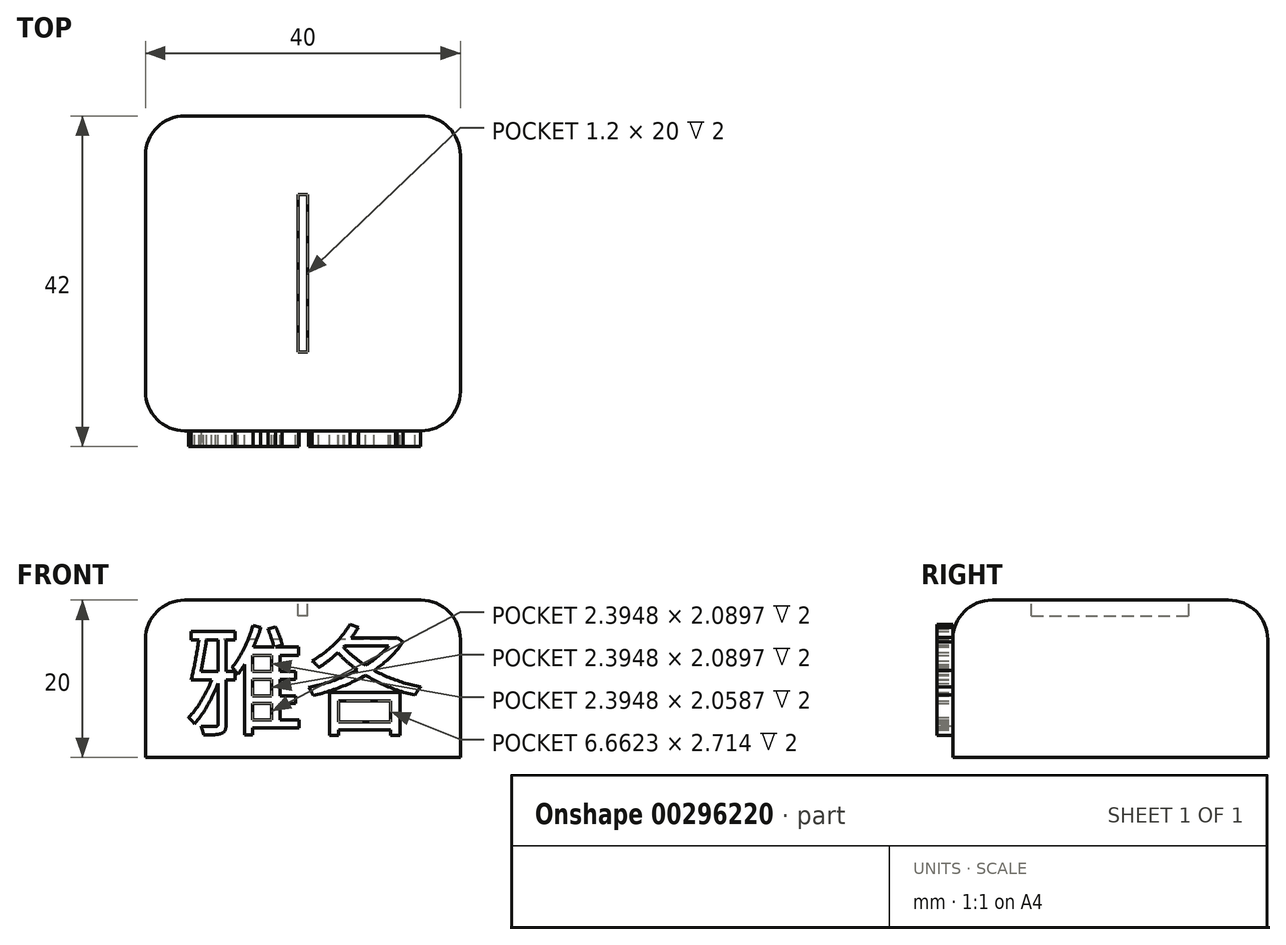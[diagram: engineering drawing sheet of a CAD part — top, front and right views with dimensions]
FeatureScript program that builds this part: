
annotation { "Feature Type Name" : "Feature", "Feature Type Description" : "" }
export const myFeature = defineFeature(function(context is Context, id is Id, definition is map)
    precondition{}
    {
        {
            var Q0;
            Q0=qCreatedBy(makeId("Top.planeOp"),FACE);
            var sketch = newSketch(context, id + "F0", { "sketchPlane" : qUnion([Q0])});
            skLineSegment(sketch, "E0.bottom", {"start": v(20, -20) * mm, "end": v(-20, -20) * mm});
            skLineSegment(sketch, "E0.top", {"start": v(20, 20) * mm, "end": v(-20, 20) * mm});
            skLineSegment(sketch, "E0.left", {"start": v(20, -20) * mm, "end": v(20, 20) * mm});
            skLineSegment(sketch, "E0.right", {"start": v(-20, -20) * mm, "end": v(-20, 20) * mm});
            skPoint(sketch, "E0.middle", {"position": v(0, 0) * mm});
            skLineSegment(sketch, "E1.bottom", {"start": v(0.6, -10) * mm, "end": v(-0.6, -10) * mm});
            skLineSegment(sketch, "E1.top", {"start": v(0.6, 10) * mm, "end": v(-0.6, 10) * mm});
            skLineSegment(sketch, "E1.left", {"start": v(0.6, -10) * mm, "end": v(0.6, 10) * mm});
            skLineSegment(sketch, "E1.right", {"start": v(-0.6, -10) * mm, "end": v(-0.6, 10) * mm});
            skSolve(sketch);
        }
        {
            var Q0;
            Q0=makeQuery(id+"F0.imprint","IMPRINT",FACE,{"disambiguationData":[TD([[makeQuery(id+"F0.imprint","IMPRINT",EDGE,{"derivedFrom":sQuery(id+"F0.wireOp",EDGE,"E0.bottom")}),-1.0]])]});
            var Q1;
            Q1=makeQuery(id+"F0.imprint","IMPRINT",FACE,{"disambiguationData":[TD([[makeQuery(id+"F0.imprint","IMPRINT",EDGE,{"derivedFrom":sQuery(id+"F0.wireOp",EDGE,"E1.bottom")}),-1.0]])]});
            extrude(context, id + "F1", {"entities" : qUnion([Q0, Q1]), "oppositeDirection" : true, "depth" : 20 * mm});
        }
        {
            var Q0;
            Q0=makeQuery(id+"F0.imprint","IMPRINT",FACE,{"disambiguationData":[TD([[makeQuery(id+"F0.imprint","IMPRINT",EDGE,{"derivedFrom":sQuery(id+"F0.wireOp",EDGE,"E1.bottom")}),-1.0]])]});
            extrude(context, id + "F2", {"entities" : qUnion([Q0]), "operationType" : NewBodyOperationType.REMOVE, "oppositeDirection" : true, "depth" : 2 * mm});
        }
        {
            var Q0;
            Q0=makeQuery(id+"F2.boolean.opBoolean","COPY",EDGE,{"derivedFrom":makeQuery(id+"F2.opExtrude","CAP_EDGE",EDGE,{"disambiguationData":[OSD([sQuery(id+"F0.wireOp",EDGE,"E1.left")])],"isStart":true})});
            var Q1;
            Q1=makeQuery(id+"F2.boolean.opBoolean","COPY",EDGE,{"derivedFrom":makeQuery(id+"F2.opExtrude","CAP_EDGE",EDGE,{"disambiguationData":[OSD([sQuery(id+"F0.wireOp",EDGE,"E1.right")])],"isStart":true})});
            var Q2;
            Q2=makeQuery(id+"F1.opExtrude","SWEPT_EDGE",EDGE,{"disambiguationData":[OSD([sQuery(id+"F0.wireOp",EDGE,"E0.bottom"),sQuery(id+"F0.wireOp",EDGE,"E0.left")])]});
            var Q3;
            Q3=makeQuery(id+"F1.opExtrude","SWEPT_EDGE",EDGE,{"disambiguationData":[OSD([sQuery(id+"F0.wireOp",EDGE,"E0.top"),sQuery(id+"F0.wireOp",EDGE,"E0.left")])]});
            var Q4;
            Q4=makeQuery(id+"F1.opExtrude","CAP_EDGE",EDGE,{"disambiguationData":[OSD([sQuery(id+"F0.wireOp",EDGE,"E0.left")])],"isStart":true});
            var Q5;
            Q5=makeQuery(id+"F1.opExtrude","SWEPT_EDGE",EDGE,{"disambiguationData":[OSD([sQuery(id+"F0.wireOp",EDGE,"E0.bottom"),sQuery(id+"F0.wireOp",EDGE,"E0.right")])]});
            var Q6;
            Q6=makeQuery(id+"F1.opExtrude","SWEPT_EDGE",EDGE,{"disambiguationData":[OSD([sQuery(id+"F0.wireOp",EDGE,"E0.top"),sQuery(id+"F0.wireOp",EDGE,"E0.right")])]});
            var Q7;
            Q7=makeQuery(id+"F1.opExtrude","CAP_EDGE",EDGE,{"disambiguationData":[OSD([sQuery(id+"F0.wireOp",EDGE,"E0.top")])],"isStart":true});
            var Q8;
            Q8=makeQuery(id+"F1.opExtrude","CAP_EDGE",EDGE,{"disambiguationData":[OSD([sQuery(id+"F0.wireOp",EDGE,"E0.right")])],"isStart":true});
            var Q9;
            Q9=makeQuery(id+"F1.opExtrude","CAP_EDGE",EDGE,{"disambiguationData":[OSD([sQuery(id+"F0.wireOp",EDGE,"E0.bottom")])],"isStart":true});
            fillet(context, id + "F3", {"entities" : qUnion([Q0, Q1, Q2, Q3, Q4, Q5, Q6, Q7, Q8, Q9]), "radius" : 5 * mm, "tangentPropagation" : true, "allowEdgeOverflow" : false});
        }
        {
            var Q0;
            Q0=makeQuery(id+"F1.opExtrude","SWEPT_FACE",FACE,{"disambiguationData":[OSD([sQuery(id+"F0.wireOp",EDGE,"E0.bottom")])]});
            var sketch = newSketch(context, id + "F4", { "sketchPlane" : qUnion([Q0])});
            skText(sketch, "E2", { "text": "雅各", "fontName": "NotoSansCJKtc-Regular.otf"});
            const initialGuessF4  = {"E2": [-0.015, -0.01598, 1, 0, 0.01098]};
            skSetInitialGuess(sketch, initialGuessF4);
            skSolve(sketch);
        }
        {
            var Q0;
            Q0=qSketchRegion(id+"F4",true);
            extrude(context, id + "F5", {"entities" : qUnion([Q0]), "operationType" : NewBodyOperationType.ADD, "depth" : 2 * mm});
        }
    });
